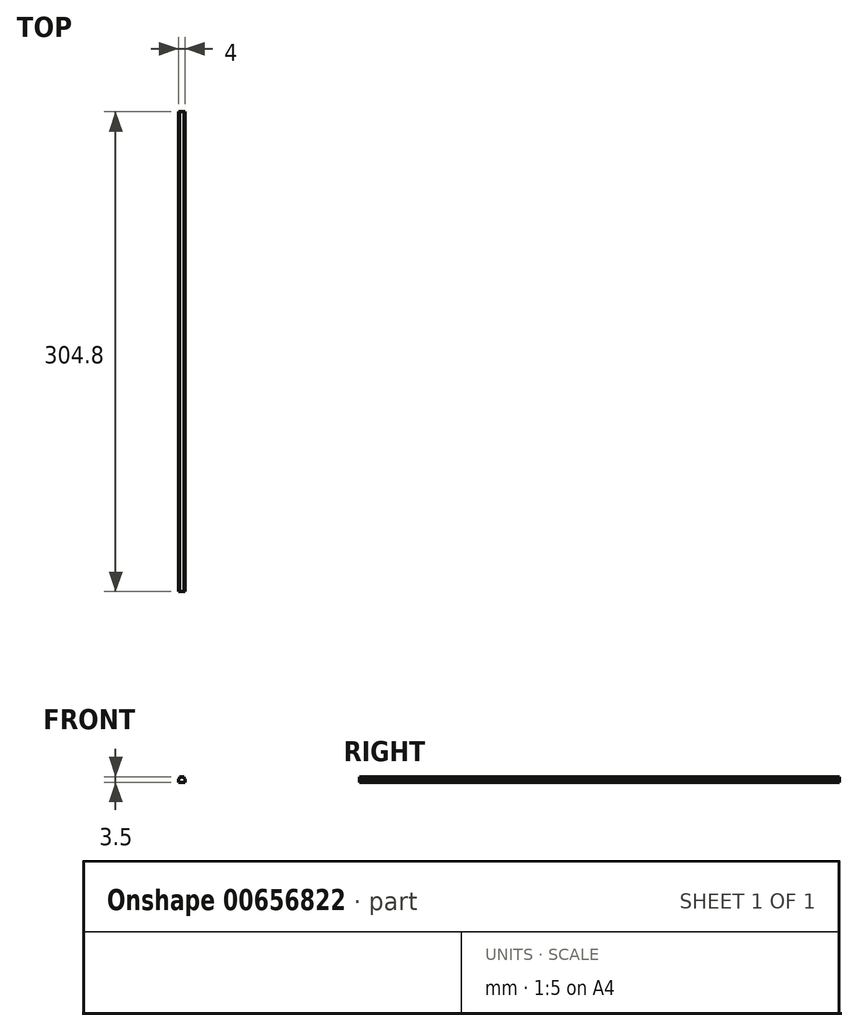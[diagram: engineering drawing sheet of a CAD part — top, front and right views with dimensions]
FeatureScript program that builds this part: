
annotation { "Feature Type Name" : "Feature", "Feature Type Description" : "" }
export const myFeature = defineFeature(function(context is Context, id is Id, definition is map)
    precondition{}
    {
        {
            var Q0;
            Q0=qCreatedBy(makeId("Front.planeOp"),FACE);
            var sketch = newSketch(context, id + "F0", { "sketchPlane" : qUnion([Q0])});
            skLineSegment(sketch, "E0", {"start": v(2, 0) * mm, "end": v(2, -2) * mm});
            skLineSegment(sketch, "E1", {"start": v(0, 0) * mm, "end": v(0, 1.5) * mm});
            skLineSegment(sketch, "E2", {"start": v(0, 1.5) * mm, "end": v(1.5, 1.5) * mm});
            skLineSegment(sketch, "E3", {"start": v(1.5, 1.5) * mm, "end": v(1.5, 0) * mm});
            skLineSegment(sketch, "E4", {"start": v(0, 0) * mm, "end": v(0, -2) * mm});
            skLineSegment(sketch, "E5", {"start": v(2, -2) * mm, "end": v(0, -2) * mm});
            skLineSegment(sketch, "E6", {"start": v(1.5, 0) * mm, "end": v(2, 0) * mm});
            skLineSegment(sketch, "E7.MirrorCS", {"start": v(-1.5, 0) * mm, "end": v(-2, 0) * mm});
            skLineSegment(sketch, "E8.MirrorCS", {"start": v(0, 1.5) * mm, "end": v(-1.5, 1.5) * mm});
            skLineSegment(sketch, "E9.MirrorCS", {"start": v(-1.5, 1.5) * mm, "end": v(-1.5, 0) * mm});
            skLineSegment(sketch, "E10.MirrorCS", {"start": v(-2, -2) * mm, "end": v(0, -2) * mm});
            skLineSegment(sketch, "E11.MirrorCS", {"start": v(-2, 0) * mm, "end": v(-2, -2) * mm});
            skSolve(sketch);
        }
        {
            var Q0;
            Q0=makeQuery(id+"F0.imprint","IMPRINT",FACE,{"disambiguationData":[TD([[makeQuery(id+"F0.imprint","IMPRINT",EDGE,{"derivedFrom":sQuery(id+"F0.wireOp",EDGE,"E7.MirrorCS")}),1.0]])]});
            var Q1;
            Q1=makeQuery(id+"F0.imprint","IMPRINT",FACE,{"disambiguationData":[TD([[makeQuery(id+"F0.imprint","IMPRINT",EDGE,{"derivedFrom":sQuery(id+"F0.wireOp",EDGE,"E0")}),-1.0]])]});
            extrude(context, id + "F1", {"entities" : qUnion([Q0, Q1]), "oppositeDirection" : true, "depth" : 304.8 * mm, "offsetDistance" : 25.4 * mm});
        }
    });
